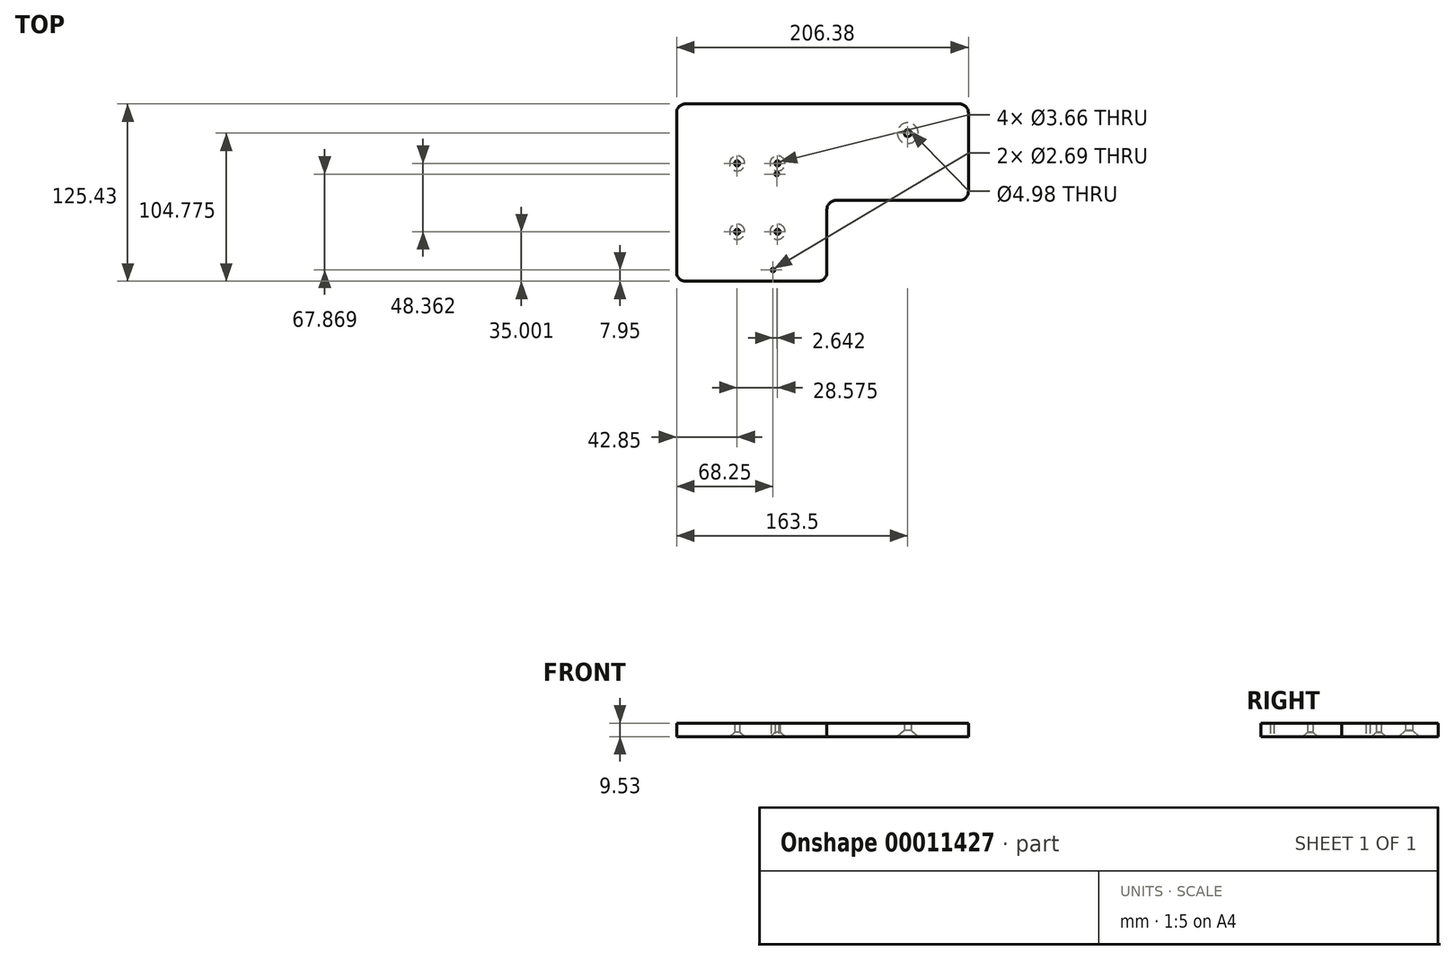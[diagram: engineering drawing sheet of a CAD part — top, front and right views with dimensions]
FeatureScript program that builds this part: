
annotation { "Feature Type Name" : "Feature", "Feature Type Description" : "" }
export const myFeature = defineFeature(function(context is Context, id is Id, definition is map)
    precondition{}
    {
        {
            var Q0;
            Q0=qCreatedBy(makeId("Top.planeOp"),FACE);
            var sketch = newSketch(context, id + "F0", { "sketchPlane" : qUnion([Q0])});
            skLineSegment(sketch, "E0", {"start": v(0, 6.35) * mm, "end": v(0, 119.08) * mm});
            skLineSegment(sketch, "E1", {"start": v(6.35, 125.43) * mm, "end": v(200.03, 125.43) * mm});
            skLineSegment(sketch, "E2", {"start": v(206.38, 119.08) * mm, "end": v(206.38, 63.5) * mm});
            skLineSegment(sketch, "E3", {"start": v(200.03, 57.15) * mm, "end": v(112.7, 57.15) * mm});
            skLineSegment(sketch, "E4", {"start": v(106.35, 50.8) * mm, "end": v(106.35, 6.35) * mm});
            skLineSegment(sketch, "E5", {"start": v(100, 0) * mm, "end": v(6.35, 0) * mm});
            skPoint(sketch, "E6.visualSharp", {"position": v(0, 125.43) * mm});
            skArc(sketch, "E6.filletArc", {"start": v(6.35, 125.43) * mm, "mid": v(1.86, 123.57) * mm, "end": v(0, 119.08) * mm});
            skPoint(sketch, "E7.visualSharp", {"position": v(206.38, 125.43) * mm});
            skArc(sketch, "E7.filletArc", {"start": v(206.38, 119.08) * mm, "mid": v(204.52, 123.57) * mm, "end": v(200.03, 125.43) * mm});
            skPoint(sketch, "E8.visualSharp", {"position": v(206.38, 57.15) * mm});
            skArc(sketch, "E8.filletArc", {"start": v(200.03, 57.15) * mm, "mid": v(204.52, 59) * mm, "end": v(206.38, 63.5) * mm});
            skPoint(sketch, "E9.visualSharp", {"position": v(106.35, 57.15) * mm});
            skArc(sketch, "E9.filletArc", {"start": v(112.7, 57.15) * mm, "mid": v(108.2, 55.3) * mm, "end": v(106.35, 50.8) * mm});
            skPoint(sketch, "E10.visualSharp", {"position": v(106.35, 0) * mm});
            skArc(sketch, "E10.filletArc", {"start": v(100, 0) * mm, "mid": v(104.49, 1.86) * mm, "end": v(106.35, 6.35) * mm});
            skPoint(sketch, "E11.visualSharp", {"position": v(0, 0) * mm});
            skArc(sketch, "E11.filletArc", {"start": v(0, 6.35) * mm, "mid": v(1.86, 1.86) * mm, "end": v(6.35, 0) * mm});
            skCircle(sketch, "E12", {"center": v(163.5, 104.78) * mm, "radius": 2.49 * mm});
            skLineSegment(sketch, "E13.bottom", {"start": v(42.85, 83.36) * mm, "end": v(71.42, 83.36) * mm, "construction": true});
            skLineSegment(sketch, "E13.top", {"start": v(42.85, 35) * mm, "end": v(71.42, 35) * mm, "construction": true});
            skLineSegment(sketch, "E13.left", {"start": v(42.85, 83.36) * mm, "end": v(42.85, 35) * mm, "construction": true});
            skLineSegment(sketch, "E13.right", {"start": v(71.42, 83.36) * mm, "end": v(71.42, 35) * mm, "construction": true});
            skCircle(sketch, "E14", {"center": v(68.25, 7.95) * mm, "radius": 1.35 * mm});
            skCircle(sketch, "E15", {"center": v(70.9, 75.82) * mm, "radius": 1.35 * mm});
            skCircle(sketch, "E16", {"center": v(42.85, 83.36) * mm, "radius": 1.83 * mm});
            skCircle(sketch, "E17", {"center": v(71.42, 83.36) * mm, "radius": 1.83 * mm});
            skCircle(sketch, "E18", {"center": v(71.42, 35) * mm, "radius": 1.83 * mm});
            skCircle(sketch, "E19", {"center": v(42.85, 35) * mm, "radius": 1.83 * mm});
            skSolve(sketch);
        }
        {
            var Q0;
            Q0 = qSketchRegion(id + "F0", true);
            extrude(context, id + "F1", {"entities" : qUnion([Q0]), "depth" : 9.52 * mm});
        }
        {
            var Q0;
            Q0=makeQuery(id+"F1.opExtrude","CAP_EDGE",EDGE,{"disambiguationData":[OSD([sQuery(id+"F0.wireOp",EDGE,"E12")])],"isStart":true});
            chamfer(context, id + "F2", {"entities" : qUnion([Q0]), "chamferType" : ChamferType.OFFSET_ANGLE, "width" : 4.89 * mm, "oppositeDirection" : false, "angle" : 41 * degree, "tangentPropagation" : true});
        }
        {
            var Q0;
            Q0=makeQuery(id+"F1.opExtrude","CAP_EDGE",EDGE,{"disambiguationData":[OSD([sQuery(id+"F0.wireOp",EDGE,"E16")])],"isStart":true});
            var Q1;
            Q1=makeQuery(id+"F1.opExtrude","CAP_EDGE",EDGE,{"disambiguationData":[OSD([sQuery(id+"F0.wireOp",EDGE,"E19")])],"isStart":true});
            var Q2;
            Q2=makeQuery(id+"F1.opExtrude","CAP_EDGE",EDGE,{"disambiguationData":[OSD([sQuery(id+"F0.wireOp",EDGE,"E18")])],"isStart":true});
            var Q3;
            Q3=makeQuery(id+"F1.opExtrude","CAP_EDGE",EDGE,{"disambiguationData":[OSD([sQuery(id+"F0.wireOp",EDGE,"E17")])],"isStart":true});
            chamfer(context, id + "F3", {"entities" : qUnion([Q0, Q1, Q2, Q3]), "chamferType" : ChamferType.OFFSET_ANGLE, "width" : 3.54 * mm, "oppositeDirection" : false, "angle" : 41 * degree, "tangentPropagation" : true});
        }
    });
